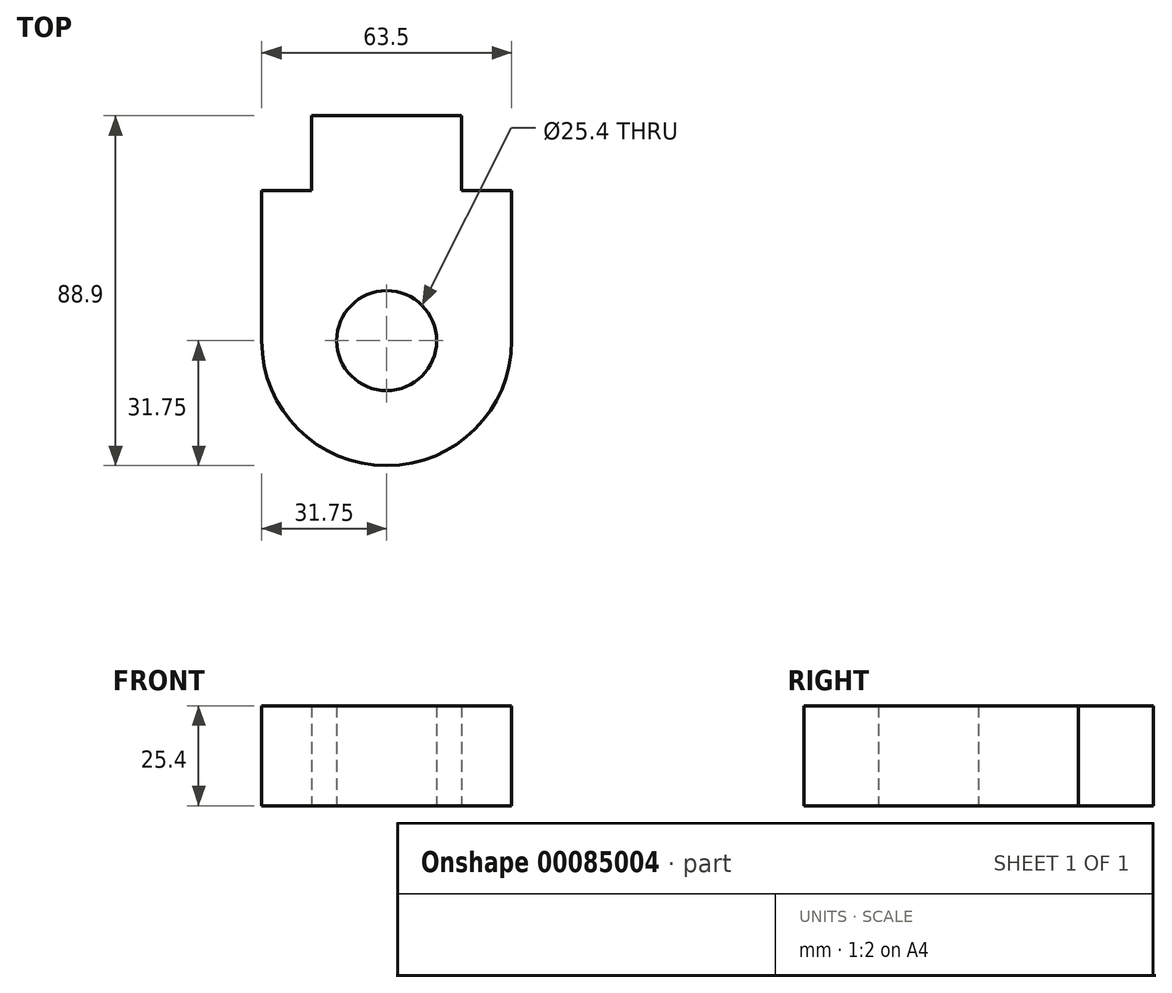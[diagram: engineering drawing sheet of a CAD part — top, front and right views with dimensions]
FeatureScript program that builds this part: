
annotation { "Feature Type Name" : "Feature", "Feature Type Description" : "" }
export const myFeature = defineFeature(function(context is Context, id is Id, definition is map)
    precondition{}
    {
        {
            var Q0;
            Q0=qCreatedBy(makeId("Top.planeOp"),FACE);
            var sketch = newSketch(context, id + "F0", { "sketchPlane" : qUnion([Q0])});
            skCircle(sketch, "E0", {"center": v(0, 0) * mm, "radius": 12.7 * mm});
            skArc(sketch, "E1", {"start": v(-31.75, 0) * mm, "mid": v(0, -31.75) * mm, "end": v(31.75, 0) * mm});
            skLineSegment(sketch, "E2", {"start": v(-31.75, 0) * mm, "end": v(-31.75, 38.1) * mm});
            skLineSegment(sketch, "E3", {"start": v(31.75, 0) * mm, "end": v(31.75, 38.1) * mm});
            skLineSegment(sketch, "E4", {"start": v(31.75, 38.1) * mm, "end": v(19.05, 38.1) * mm});
            skLineSegment(sketch, "E5", {"start": v(19.05, 38.1) * mm, "end": v(19.05, 57.15) * mm});
            skLineSegment(sketch, "E6", {"start": v(19.05, 57.15) * mm, "end": v(-19.05, 57.15) * mm});
            skLineSegment(sketch, "E7", {"start": v(-19.05, 57.15) * mm, "end": v(-19.05, 38.1) * mm});
            skLineSegment(sketch, "E8", {"start": v(-19.05, 38.1) * mm, "end": v(-31.75, 38.1) * mm});
            skSolve(sketch);
        }
        {
            var Q0;
            Q0 = qSketchRegion(id + "F0", true);
            extrude(context, id + "F1", {"entities" : qUnion([Q0]), "depth" : 25.4 * mm});
        }
    });
